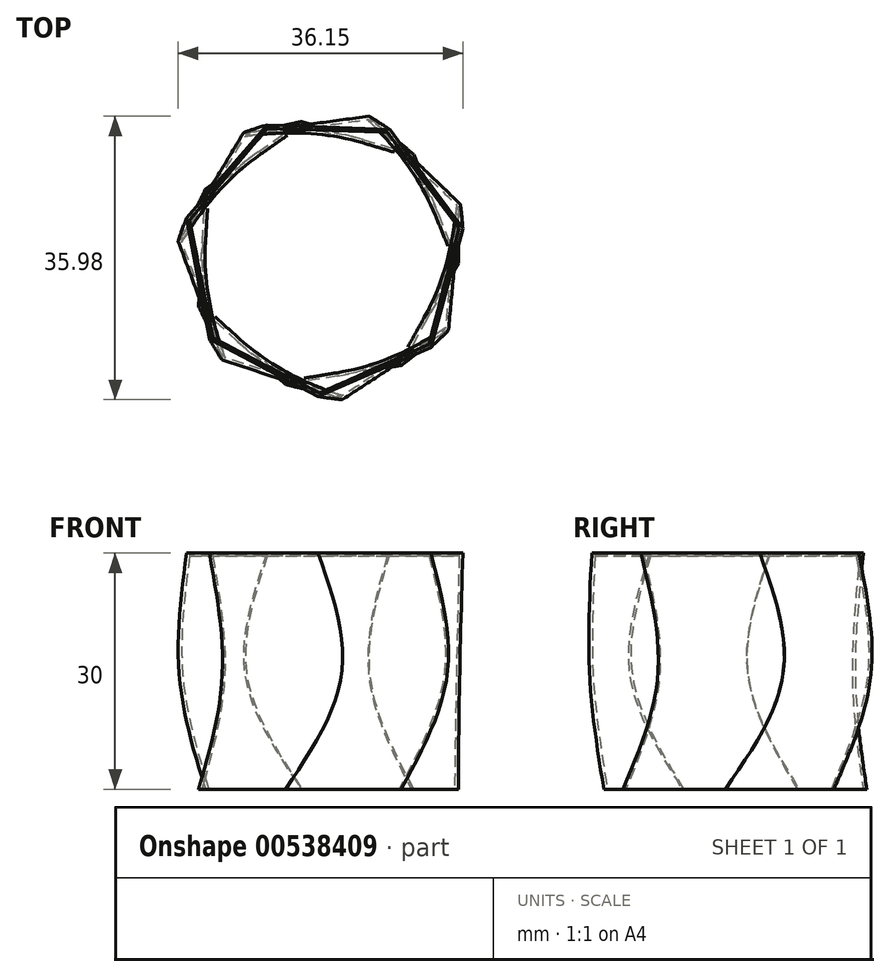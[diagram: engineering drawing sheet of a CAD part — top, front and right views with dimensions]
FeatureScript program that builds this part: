
annotation { "Feature Type Name" : "Feature", "Feature Type Description" : "" }
export const myFeature = defineFeature(function(context is Context, id is Id, definition is map)
    precondition{}
    {
        {
            var Q0;
            Q0=qCreatedBy(makeId("Top.planeOp"),FACE);
            cPlane(context, id + "F0", {"entities" : qUnion([Q0]), "cplaneType" : CPlaneType.OFFSET, "offset" : 15 * mm, "width" : 150 * mm, "height" : 150 * mm});
        }
        {
            var Q0;
            Q0=qCreatedBy(makeId("Top.planeOp"),FACE);
            var sketch = newSketch(context, id + "F1", { "sketchPlane" : qUnion([Q0])});
            skCircle(sketch, "E0.cCircle", {"center": v(0, 0) * mm, "radius": 16.62 * mm, "construction": true});
            skLineSegment(sketch, "E0.0", {"start": v(-18.36, 1.78) * mm, "end": v(-10.05, 15.46) * mm});
            skLineSegment(sketch, "E0.1", {"start": v(-10.05, 15.46) * mm, "end": v(5.82, 17.5) * mm});
            skLineSegment(sketch, "E0.2", {"start": v(5.82, 17.5) * mm, "end": v(17.31, 6.36) * mm});
            skLineSegment(sketch, "E0.3", {"start": v(17.31, 6.36) * mm, "end": v(15.76, -9.57) * mm});
            skLineSegment(sketch, "E0.4", {"start": v(15.76, -9.57) * mm, "end": v(2.35, -18.3) * mm});
            skLineSegment(sketch, "E0.5", {"start": v(2.35, -18.3) * mm, "end": v(-12.84, -13.24) * mm});
            skLineSegment(sketch, "E0.6", {"start": v(-12.84, -13.24) * mm, "end": v(-18.36, 1.78) * mm});
            skPoint(sketch, "E0.0.midPoint", {"position": v(-14.2, 8.62) * mm});
            skSolve(sketch);
        }
        {
            var Q0;
            Q0=qCreatedBy(id+"F0.planeOp",FACE);
            var sketch = newSketch(context, id + "F2", { "sketchPlane" : qUnion([Q0])});
            skCircle(sketch, "E1.cCircle", {"center": v(0, 0) * mm, "radius": 16.22 * mm, "construction": true});
            skLineSegment(sketch, "E1.0", {"start": v(13.64, -11.75) * mm, "end": v(-0.68, -18) * mm});
            skLineSegment(sketch, "E1.1", {"start": v(-0.68, -18) * mm, "end": v(-14.5, -10.69) * mm});
            skLineSegment(sketch, "E1.2", {"start": v(-14.5, -10.69) * mm, "end": v(-17.4, 4.67) * mm});
            skLineSegment(sketch, "E1.3", {"start": v(-17.4, 4.67) * mm, "end": v(-7.2, 16.5) * mm});
            skLineSegment(sketch, "E1.4", {"start": v(-7.2, 16.5) * mm, "end": v(8.42, 15.92) * mm});
            skLineSegment(sketch, "E1.5", {"start": v(8.42, 15.92) * mm, "end": v(17.7, 3.34) * mm});
            skLineSegment(sketch, "E1.6", {"start": v(17.7, 3.34) * mm, "end": v(13.64, -11.75) * mm});
            skPoint(sketch, "E1.0.midPoint", {"position": v(6.48, -14.87) * mm});
            skSolve(sketch);
        }
        {
            var Q0;
            Q0=qCreatedBy(makeId("Top.planeOp"),FACE);
            cPlane(context, id + "F3", {"entities" : qUnion([Q0]), "cplaneType" : CPlaneType.OFFSET, "offset" : 15 * mm, "oppositeDirection" : true, "width" : 150 * mm, "height" : 150 * mm});
        }
        {
            var Q0;
            Q0=qCreatedBy(id+"F3.planeOp",FACE);
            var sketch = newSketch(context, id + "F4", { "sketchPlane" : qUnion([Q0])});
            skCircle(sketch, "E2.cCircle", {"center": v(0, 0) * mm, "radius": 15.46 * mm, "construction": true});
            skLineSegment(sketch, "E2.0", {"start": v(11.49, 12.75) * mm, "end": v(17.13, -1.03) * mm});
            skLineSegment(sketch, "E2.1", {"start": v(17.13, -1.03) * mm, "end": v(9.87, -14.03) * mm});
            skLineSegment(sketch, "E2.2", {"start": v(9.87, -14.03) * mm, "end": v(-4.82, -16.47) * mm});
            skLineSegment(sketch, "E2.3", {"start": v(-4.82, -16.47) * mm, "end": v(-15.88, -6.5) * mm});
            skLineSegment(sketch, "E2.4", {"start": v(-15.88, -6.5) * mm, "end": v(-14.98, 8.36) * mm});
            skLineSegment(sketch, "E2.5", {"start": v(-14.98, 8.36) * mm, "end": v(-2.8, 16.93) * mm});
            skLineSegment(sketch, "E2.6", {"start": v(-2.8, 16.93) * mm, "end": v(11.49, 12.75) * mm});
            skPoint(sketch, "E2.0.midPoint", {"position": v(14.3, 5.86) * mm});
            skSolve(sketch);
        }
        {
            var Q0;
            Q0=makeQuery(id+"F2.imprint","IMPRINT",FACE,{"disambiguationData":[TD([[makeQuery(id+"F2.imprint","IMPRINT",EDGE,{"derivedFrom":sQuery(id+"F2.wireOp",EDGE,"E1.0")}),-1.0]])]});
            var Q1;
            Q1=makeQuery(id+"F1.imprint","IMPRINT",FACE,{"disambiguationData":[TD([[makeQuery(id+"F1.imprint","IMPRINT",EDGE,{"derivedFrom":sQuery(id+"F1.wireOp",EDGE,"E0.0")}),-1.0]])]});
            var Q2;
            Q2=makeQuery(id+"F4.imprint","IMPRINT",FACE,{"disambiguationData":[TD([[makeQuery(id+"F4.imprint","IMPRINT",EDGE,{"derivedFrom":sQuery(id+"F4.wireOp",EDGE,"E2.0")}),-1.0]])]});
            loft(context, id + "F5", {"sheetProfilesArray" : [{ "sheetProfileEntities" : qUnion([Q0]) }, { "sheetProfileEntities" : qUnion([Q1]) }, { "sheetProfileEntities" : qUnion([Q2]) }]});
        }
        {
            var Q0;
            Q0=makeQuery(id+"F5.opLoft","CAP_FACE",FACE,{"disambiguationData":[OSD([makeQuery(id+"F4.imprint","IMPRINT",FACE,{"disambiguationData":[TD([[makeQuery(id+"F4.imprint","IMPRINT",EDGE,{"derivedFrom":sQuery(id+"F4.wireOp",EDGE,"E2.0")}),-1.0]])]})])],"isStart":true});
            shell(context, id + "F6", {"entities" : qUnion([Q0]), "thickness" : 0.4 * mm});
        }
        {
            var Q0;
            Q0=makeQuery(id+"F6.opShell","OFFSET_FACE",FACE,{"disambiguationData":[OSD([makeQuery(id+"F2.imprint","IMPRINT",FACE,{"disambiguationData":[TD([[makeQuery(id+"F2.imprint","IMPRINT",EDGE,{"derivedFrom":sQuery(id+"F2.wireOp",EDGE,"E1.0")}),-1.0]])]})])]});
            extrude(context, id + "F7", {"entities" : qUnion([Q0]), "operationType" : NewBodyOperationType.REMOVE, "oppositeDirection" : true, "depth" : 25 * mm, "offsetDistance" : 25 * mm});
        }
    });
